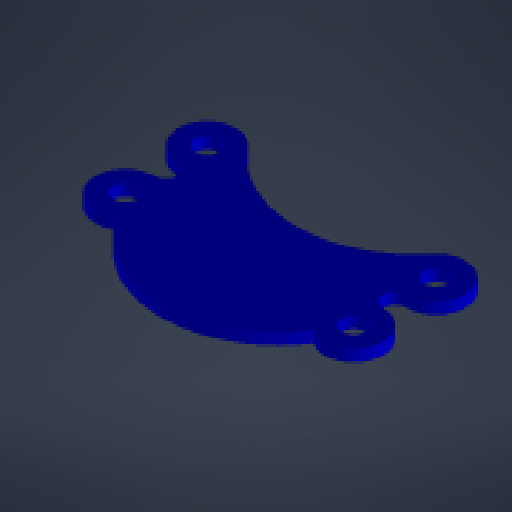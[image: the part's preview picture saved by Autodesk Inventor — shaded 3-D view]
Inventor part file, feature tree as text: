
AUTODESK INVENTOR PART (.ipt)
format: ipt  version: 2024 (Build 280153000, 153)  size: 157,696 bytes
history: native  units: mm
features: other x4, reference x4, extrude x1, sketch x1
ambient origin geometry x8: Origin, YZ Plane, XZ Plane, XY Plane, X Axis, Y Axis, Z Axis, Center Point
bodies: Body1 (feature_tree)
feature tree (10):
  other  "Твердое тело1"
  extrude  "Выдавливание1"  Depth=2.0mm
  sketch  "Эскиз1"
  reference  "Ссылка1"
  reference  "Ссылка2"
  reference  "Ссылка3"
  reference  "Ссылка4"
  parser-record x1  (decoder bookkeeping rows leaked as tree rows — omitted from the tree; the rows remain in map.json)
  other  "front_box_asembly.iam"
  other  "front_box_cup:1"
note: 1 file-system path scrubbed to <path> (originals preserved in map.json)
